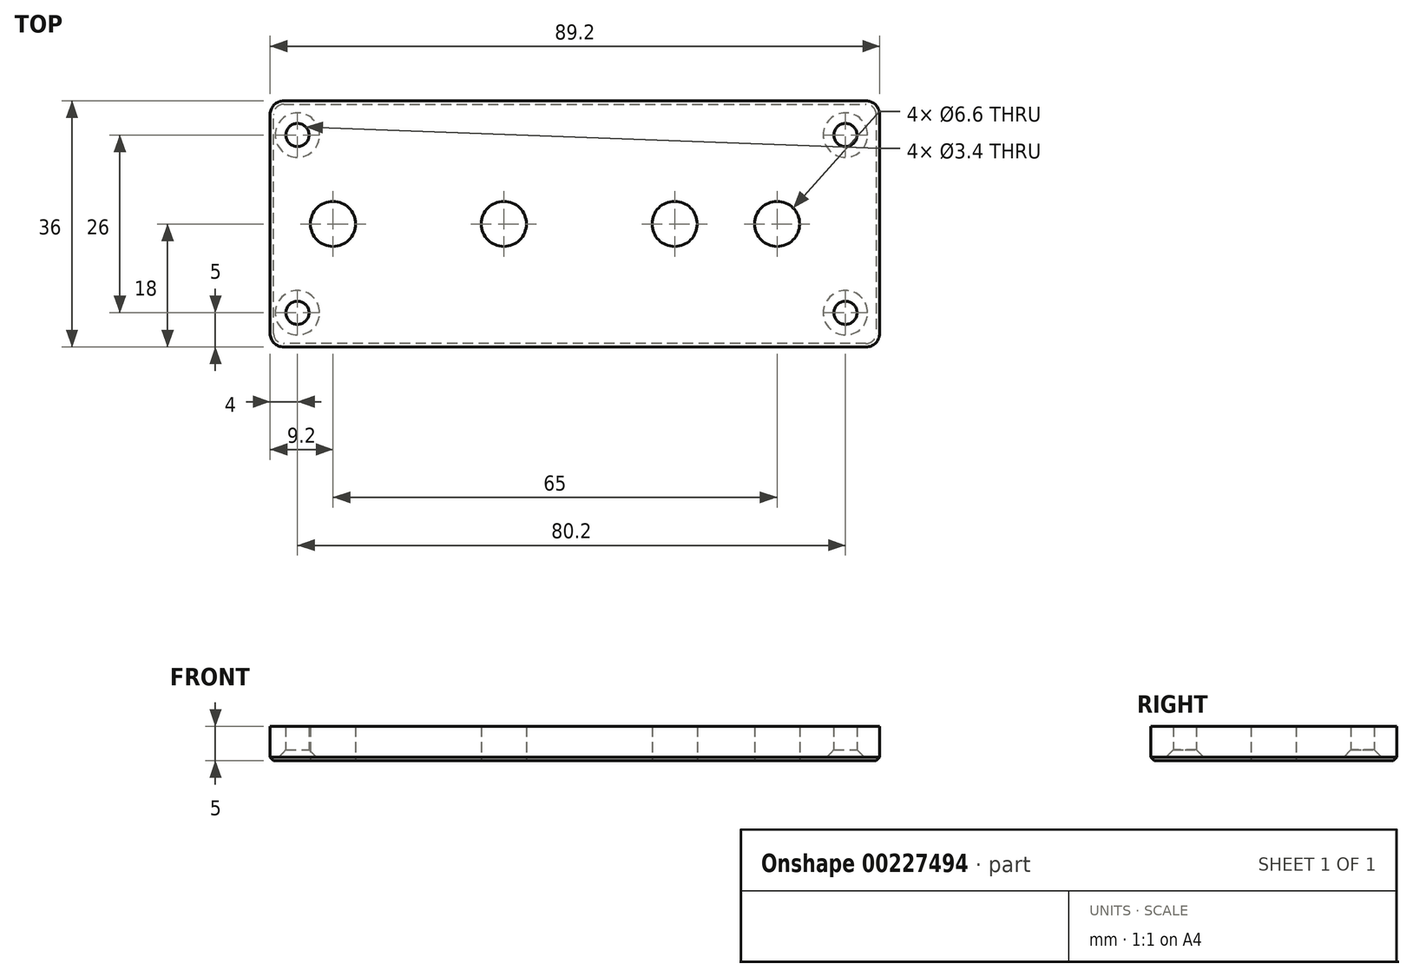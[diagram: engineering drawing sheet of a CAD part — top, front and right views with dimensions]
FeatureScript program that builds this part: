
annotation { "Feature Type Name" : "Feature", "Feature Type Description" : "" }
export const myFeature = defineFeature(function(context is Context, id is Id, definition is map)
    precondition{}
    {
        {
            var Q0;
            Q0=qCreatedBy(makeId("Top.planeOp"),FACE);
            var sketch = newSketch(context, id + "F0", { "sketchPlane" : qUnion([Q0])});
            skLineSegment(sketch, "E0.bottom", {"start": v(44.6, -18) * mm, "end": v(-44.6, -18) * mm});
            skLineSegment(sketch, "E0.top", {"start": v(44.6, 18) * mm, "end": v(-44.6, 18) * mm});
            skLineSegment(sketch, "E0.left", {"start": v(44.6, -18) * mm, "end": v(44.6, 18) * mm});
            skLineSegment(sketch, "E0.right", {"start": v(-44.6, -18) * mm, "end": v(-44.6, 18) * mm});
            skPoint(sketch, "E0.middle", {"position": v(0, 0) * mm});
            skPoint(sketch, "E1", {"position": v(29.6, 0) * mm});
            skPoint(sketch, "E2", {"position": v(14.6, 0) * mm});
            skPoint(sketch, "E3.1.0.0", {"position": v(-10.4, 0) * mm});
            skPoint(sketch, "E3.2.0.0", {"position": v(-35.4, 0) * mm});
            skLineSegment(sketch, "E3.direction1", {"start": v(14.6, 0) * mm, "end": v(-10.4, 0) * mm, "construction": true});
            skPoint(sketch, "E4", {"position": v(39.6, 13) * mm});
            skPoint(sketch, "E5.0.1.0", {"position": v(39.6, -13) * mm});
            skPoint(sketch, "E5.1.0.0", {"position": v(-40.6, 13) * mm});
            skPoint(sketch, "E5.1.1.0", {"position": v(-40.6, -13) * mm});
            skLineSegment(sketch, "E5.direction1", {"start": v(39.6, 13) * mm, "end": v(-40.6, 13) * mm, "construction": true});
            skLineSegment(sketch, "E5.direction2", {"start": v(39.6, 13) * mm, "end": v(39.6, -13) * mm, "construction": true});
            skSolve(sketch);
        }
        {
            var Q0;
            Q0=makeQuery(id+"F0.imprint","IMPRINT",FACE,{"disambiguationData":[TD([[makeQuery(id+"F0.imprint","IMPRINT",EDGE,{"derivedFrom":sQuery(id+"F0.wireOp",EDGE,"E0.bottom")}),-1.0]])]});
            extrude(context, id + "F1", {"entities" : qUnion([Q0]), "depth" : 5 * mm});
        }
        {
            var Q0;
            Q0=sQuery(id+"F0.wireOp",VERTEX,"E3.2.0.0");
            var Q1;
            Q1=sQuery(id+"F0.wireOp",VERTEX,"E3.1.0.0");
            var Q2;
            Q2=sQuery(id+"F0.wireOp",VERTEX,"E2");
            var Q3;
            Q3=sQuery(id+"F0.wireOp",VERTEX,"E1");
            var Q4;
            Q4=makeQuery(id+"F1.opExtrude","SWEPT_BODY",BODY,{"disambiguationData":[OSD([sQuery(id+"F0.wireOp",EDGE,"E0.bottom"),sQuery(id+"F0.wireOp",EDGE,"E0.top"),sQuery(id+"F0.wireOp",EDGE,"E0.left"),sQuery(id+"F0.wireOp",EDGE,"E0.right")])]});
            hole(context, id + "F2", {"style" : HoleStyle.SIMPLE, "endStyle" : HoleEndStyle.BLIND, "oppositeDirection" : true, "standardTappedOrClearance" : lookupTablePath({ "standard" : "ISO", "fit" : "Normal", "size" : "M6", "type" : "Clearance" }), "standardBlindInLast" : lookupTablePath({ "fit" : "Standard", "standard" : "ISO", "size" : "M6", "type" : "Clearance" }), "holeDiameter" : 6.6 * mm, "holeDepth" : 15 * mm, "locations" : qUnion([Q0, Q1, Q2, Q3]), "scope" : qUnion([Q4])});
        }
        {
            var Q0;
            Q0=sQuery(id+"F0.wireOp",VERTEX,"E5.1.1.0");
            var Q1;
            Q1=sQuery(id+"F0.wireOp",VERTEX,"E5.1.0.0");
            var Q2;
            Q2=sQuery(id+"F0.wireOp",VERTEX,"E4");
            var Q3;
            Q3=sQuery(id+"F0.wireOp",VERTEX,"E5.0.1.0");
            var Q4;
            Q4=makeQuery(id+"F1.opExtrude","SWEPT_BODY",BODY,{"disambiguationData":[OSD([sQuery(id+"F0.wireOp",EDGE,"E0.bottom"),sQuery(id+"F0.wireOp",EDGE,"E0.top"),sQuery(id+"F0.wireOp",EDGE,"E0.left"),sQuery(id+"F0.wireOp",EDGE,"E0.right")])]});
            hole(context, id + "F3", {"style" : HoleStyle.C_SINK, "endStyle" : HoleEndStyle.BLIND, "oppositeDirection" : true, "holeDiameter" : 3.4 * mm, "cSinkDiameter" : 6.5 * mm, "cSinkAngle" : 90 * degree, "holeDepth" : 15 * mm, "locations" : qUnion([Q0, Q1, Q2, Q3]), "scope" : qUnion([Q4])});
        }
        {
            var Q0;
            Q0=makeQuery(id+"F1.opExtrude","SWEPT_EDGE",EDGE,{"disambiguationData":[OSD([sQuery(id+"F0.wireOp",EDGE,"E0.top"),sQuery(id+"F0.wireOp",EDGE,"E0.right")])]});
            var Q1;
            Q1=makeQuery(id+"F1.opExtrude","SWEPT_EDGE",EDGE,{"disambiguationData":[OSD([sQuery(id+"F0.wireOp",EDGE,"E0.top"),sQuery(id+"F0.wireOp",EDGE,"E0.left")])]});
            var Q2;
            Q2=makeQuery(id+"F1.opExtrude","SWEPT_EDGE",EDGE,{"disambiguationData":[OSD([sQuery(id+"F0.wireOp",EDGE,"E0.bottom"),sQuery(id+"F0.wireOp",EDGE,"E0.right")])]});
            var Q3;
            Q3=makeQuery(id+"F1.opExtrude","SWEPT_EDGE",EDGE,{"disambiguationData":[OSD([sQuery(id+"F0.wireOp",EDGE,"E0.bottom"),sQuery(id+"F0.wireOp",EDGE,"E0.left")])]});
            fillet(context, id + "F4", {"entities" : qUnion([Q0, Q1, Q2, Q3]), "radius" : 2 * mm, "tangentPropagation" : true, "allowEdgeOverflow" : false});
        }
        {
            var Q0;
            Q0=makeQuery(id+"F1.opExtrude","CAP_EDGE",EDGE,{"disambiguationData":[OSD([sQuery(id+"F0.wireOp",EDGE,"E0.left")])],"isStart":true});
            chamfer(context, id + "F5", {"entities" : qUnion([Q0]), "width" : 0.5 * mm, "tangentPropagation" : true});
        }
    });
